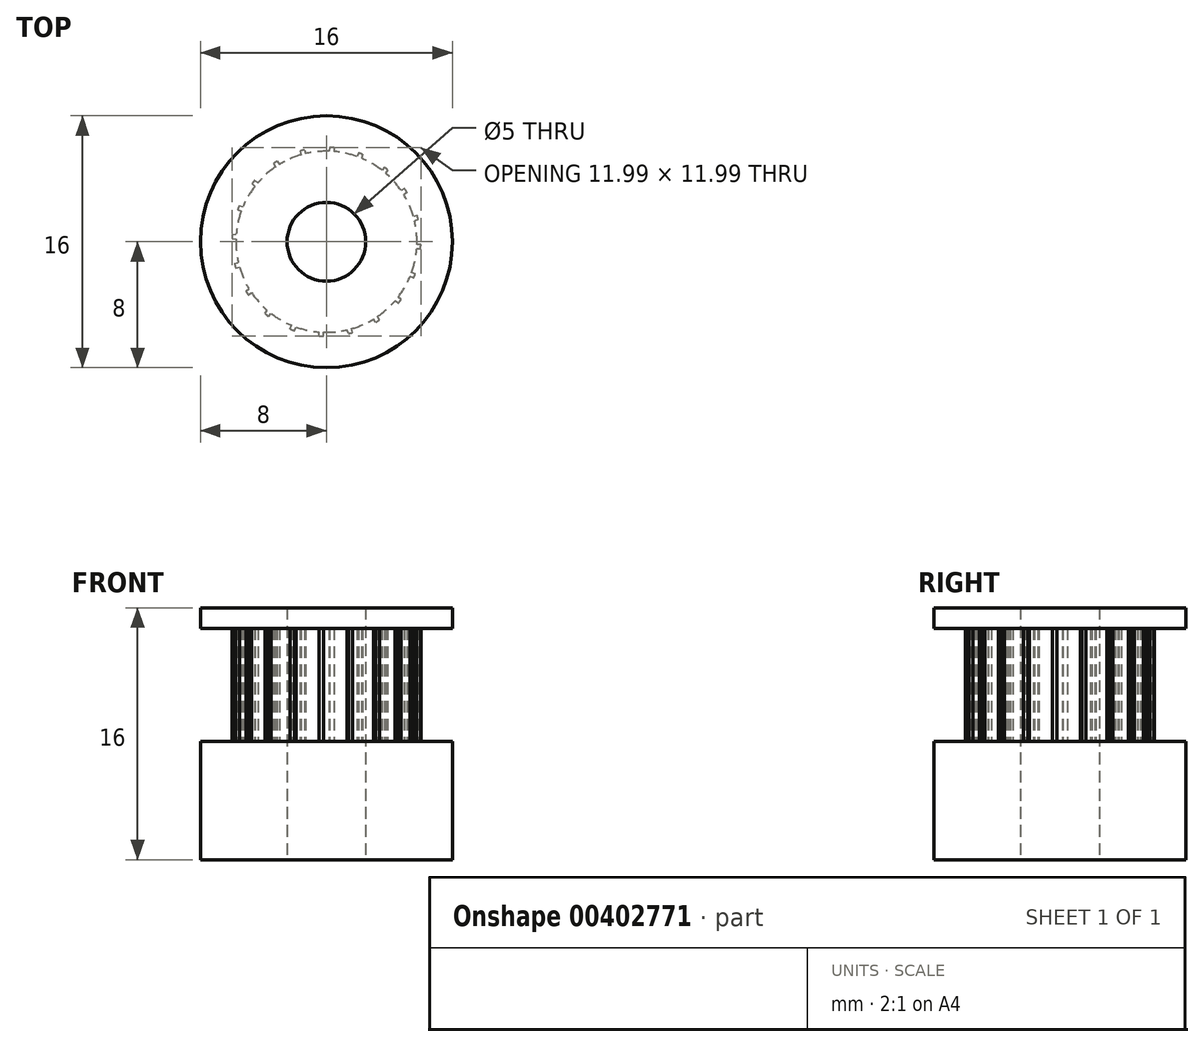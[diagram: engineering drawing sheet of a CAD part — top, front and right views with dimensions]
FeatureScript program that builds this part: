
annotation { "Feature Type Name" : "Feature", "Feature Type Description" : "" }
export const myFeature = defineFeature(function(context is Context, id is Id, definition is map)
    precondition{}
    {
        {
            var Q0;
            Q0=qCreatedBy(makeId("Top.planeOp"),FACE);
            var sketch = newSketch(context, id + "F0", { "sketchPlane" : qUnion([Q0])});
            skCircle(sketch, "E0", {"center": v(0, 0) * mm, "radius": 8 * mm});
            skCircle(sketch, "E1", {"center": v(0, 0) * mm, "radius": 2.5 * mm});
            skSolve(sketch);
        }
        {
            var Q0;
            Q0=makeQuery(id+"F0.imprint","IMPRINT",FACE,{"disambiguationData":[TD([[makeQuery(id+"F0.imprint","IMPRINT",EDGE,{"derivedFrom":sQuery(id+"F0.wireOp",EDGE,"E0")}),1.0]])]});
            extrude(context, id + "F1", {"entities" : qUnion([Q0]), "depth" : 7.5 * mm});
        }
        {
            var Q0;
            Q0=makeQuery(id+"F1.opExtrude","CAP_FACE",FACE,{"disambiguationData":[OSD([sQuery(id+"F0.wireOp",EDGE,"E0"),sQuery(id+"F0.wireOp",EDGE,"E1")])],"isStart":false});
            var sketch = newSketch(context, id + "F2", { "sketchPlane" : qUnion([Q0])});
            skArc(sketch, "E2", {"start": v(5.12, 3.13) * mm, "mid": v(5.04, 3.25) * mm, "end": v(4.96, 3.37) * mm});
            skArc(sketch, "E3", {"start": v(5.52, 1.6) * mm, "mid": v(5.26, 2.32) * mm, "end": v(4.92, 2.98) * mm});
            skLineSegment(sketch, "E4", {"start": v(4.96, 3.37) * mm, "end": v(4.75, 3.24) * mm});
            skLineSegment(sketch, "E5", {"start": v(3.9, 4.56) * mm, "end": v(3.75, 4.36) * mm});
            skLineSegment(sketch, "E6.1.0", {"start": v(2.3, 5.54) * mm, "end": v(2.22, 5.3) * mm});
            skLineSegment(sketch, "E6.1.1", {"start": v(3.68, 4.74) * mm, "end": v(3.52, 4.55) * mm});
            skLineSegment(sketch, "E6.2.0", {"start": v(0.47, 5.98) * mm, "end": v(0.48, 5.73) * mm});
            skLineSegment(sketch, "E6.2.1", {"start": v(2.04, 5.64) * mm, "end": v(1.94, 5.41) * mm});
            skLineSegment(sketch, "E6.3.0", {"start": v(-1.4, 5.83) * mm, "end": v(-1.32, 5.6) * mm});
            skLineSegment(sketch, "E6.3.1", {"start": v(0.2, 6) * mm, "end": v(0.18, 5.75) * mm});
            skLineSegment(sketch, "E6.4.0", {"start": v(-3.13, 5.12) * mm, "end": v(-2.98, 4.92) * mm});
            skLineSegment(sketch, "E6.4.1", {"start": v(-1.67, 5.76) * mm, "end": v(-1.6, 5.52) * mm});
            skLineSegment(sketch, "E6.5.0", {"start": v(-4.56, 3.9) * mm, "end": v(-4.36, 3.75) * mm});
            skLineSegment(sketch, "E6.5.1", {"start": v(-3.37, 4.96) * mm, "end": v(-3.24, 4.75) * mm});
            skLineSegment(sketch, "E6.6.0", {"start": v(-5.54, 2.3) * mm, "end": v(-5.3, 2.22) * mm});
            skLineSegment(sketch, "E6.6.1", {"start": v(-4.74, 3.68) * mm, "end": v(-4.55, 3.52) * mm});
            skLineSegment(sketch, "E6.7.0", {"start": v(-5.98, 0.47) * mm, "end": v(-5.73, 0.48) * mm});
            skLineSegment(sketch, "E6.7.1", {"start": v(-5.64, 2.04) * mm, "end": v(-5.41, 1.94) * mm});
            skLineSegment(sketch, "E6.8.0", {"start": v(-5.83, -1.4) * mm, "end": v(-5.6, -1.32) * mm});
            skLineSegment(sketch, "E6.8.1", {"start": v(-6, 0.2) * mm, "end": v(-5.75, 0.18) * mm});
            skLineSegment(sketch, "E6.9.0", {"start": v(-5.12, -3.13) * mm, "end": v(-4.92, -2.98) * mm});
            skLineSegment(sketch, "E6.9.1", {"start": v(-5.76, -1.67) * mm, "end": v(-5.52, -1.6) * mm});
            skLineSegment(sketch, "E6.10.0", {"start": v(-3.9, -4.56) * mm, "end": v(-3.75, -4.36) * mm});
            skLineSegment(sketch, "E6.10.1", {"start": v(-4.96, -3.37) * mm, "end": v(-4.75, -3.24) * mm});
            skLineSegment(sketch, "E6.11.0", {"start": v(-2.3, -5.54) * mm, "end": v(-2.22, -5.3) * mm});
            skLineSegment(sketch, "E6.11.1", {"start": v(-3.68, -4.74) * mm, "end": v(-3.52, -4.55) * mm});
            skLineSegment(sketch, "E6.12.0", {"start": v(-0.47, -5.98) * mm, "end": v(-0.48, -5.73) * mm});
            skLineSegment(sketch, "E6.12.1", {"start": v(-2.04, -5.64) * mm, "end": v(-1.94, -5.41) * mm});
            skLineSegment(sketch, "E6.13.0", {"start": v(1.4, -5.83) * mm, "end": v(1.32, -5.6) * mm});
            skLineSegment(sketch, "E6.13.1", {"start": v(-0.2, -6) * mm, "end": v(-0.18, -5.75) * mm});
            skLineSegment(sketch, "E6.14.0", {"start": v(3.13, -5.12) * mm, "end": v(2.98, -4.92) * mm});
            skLineSegment(sketch, "E6.14.1", {"start": v(1.67, -5.76) * mm, "end": v(1.6, -5.52) * mm});
            skLineSegment(sketch, "E6.15.0", {"start": v(4.56, -3.9) * mm, "end": v(4.36, -3.75) * mm});
            skLineSegment(sketch, "E6.15.1", {"start": v(3.37, -4.96) * mm, "end": v(3.24, -4.75) * mm});
            skLineSegment(sketch, "E6.16.0", {"start": v(5.54, -2.3) * mm, "end": v(5.3, -2.22) * mm});
            skLineSegment(sketch, "E6.16.1", {"start": v(4.74, -3.68) * mm, "end": v(4.55, -3.52) * mm});
            skLineSegment(sketch, "E6.17.0", {"start": v(5.98, -0.47) * mm, "end": v(5.73, -0.48) * mm});
            skLineSegment(sketch, "E6.17.1", {"start": v(5.64, -2.04) * mm, "end": v(5.41, -1.94) * mm});
            skLineSegment(sketch, "E6.18.0", {"start": v(5.83, 1.4) * mm, "end": v(5.6, 1.32) * mm});
            skLineSegment(sketch, "E6.18.1", {"start": v(6, -0.2) * mm, "end": v(5.75, -0.18) * mm});
            skLineSegment(sketch, "E6.19.0", {"start": v(5.12, 3.13) * mm, "end": v(4.92, 2.98) * mm});
            skLineSegment(sketch, "E6.19.1", {"start": v(5.76, 1.67) * mm, "end": v(5.52, 1.6) * mm});
            skArc(sketch, "E7.trimOffspring", {"start": v(3.9, 4.56) * mm, "mid": v(3.8, 4.65) * mm, "end": v(3.68, 4.74) * mm});
            skArc(sketch, "E8.trimOffspring", {"start": v(2.3, 5.54) * mm, "mid": v(2.17, 5.6) * mm, "end": v(2.04, 5.64) * mm});
            skArc(sketch, "E9.trimOffspring", {"start": v(0.47, 5.98) * mm, "mid": v(0.33, 6) * mm, "end": v(0.2, 6) * mm});
            skArc(sketch, "E10.trimOffspring", {"start": v(-1.4, 5.83) * mm, "mid": v(-1.54, 5.8) * mm, "end": v(-1.67, 5.76) * mm});
            skArc(sketch, "E11.trimOffspring", {"start": v(-3.13, 5.12) * mm, "mid": v(-3.25, 5.04) * mm, "end": v(-3.37, 4.96) * mm});
            skArc(sketch, "E12.trimOffspring", {"start": v(-4.56, 3.9) * mm, "mid": v(-4.65, 3.8) * mm, "end": v(-4.74, 3.68) * mm});
            skArc(sketch, "E13.trimOffspring", {"start": v(-5.54, 2.3) * mm, "mid": v(-5.6, 2.17) * mm, "end": v(-5.64, 2.04) * mm});
            skArc(sketch, "E14.trimOffspring", {"start": v(-5.98, 0.47) * mm, "mid": v(-6, 0.33) * mm, "end": v(-6, 0.2) * mm});
            skArc(sketch, "E15.trimOffspring", {"start": v(-5.83, -1.4) * mm, "mid": v(-5.8, -1.54) * mm, "end": v(-5.76, -1.67) * mm});
            skArc(sketch, "E16.trimOffspring", {"start": v(-5.12, -3.13) * mm, "mid": v(-5.04, -3.25) * mm, "end": v(-4.96, -3.37) * mm});
            skArc(sketch, "E17.trimOffspring", {"start": v(-3.9, -4.56) * mm, "mid": v(-3.8, -4.65) * mm, "end": v(-3.68, -4.74) * mm});
            skArc(sketch, "E18.trimOffspring", {"start": v(-2.3, -5.54) * mm, "mid": v(-2.17, -5.6) * mm, "end": v(-2.04, -5.64) * mm});
            skArc(sketch, "E19.trimOffspring", {"start": v(-0.47, -5.98) * mm, "mid": v(-0.33, -6) * mm, "end": v(-0.2, -6) * mm});
            skArc(sketch, "E20.trimOffspring", {"start": v(1.4, -5.83) * mm, "mid": v(1.54, -5.8) * mm, "end": v(1.67, -5.76) * mm});
            skArc(sketch, "E21.trimOffspring", {"start": v(3.13, -5.12) * mm, "mid": v(3.25, -5.04) * mm, "end": v(3.37, -4.96) * mm});
            skArc(sketch, "E22.trimOffspring", {"start": v(4.56, -3.9) * mm, "mid": v(4.65, -3.8) * mm, "end": v(4.74, -3.68) * mm});
            skArc(sketch, "E23.trimOffspring", {"start": v(5.54, -2.3) * mm, "mid": v(5.6, -2.17) * mm, "end": v(5.64, -2.04) * mm});
            skArc(sketch, "E24.trimOffspring", {"start": v(5.98, -0.47) * mm, "mid": v(6, -0.33) * mm, "end": v(6, -0.2) * mm});
            skArc(sketch, "E25.trimOffspring", {"start": v(5.83, 1.4) * mm, "mid": v(5.8, 1.54) * mm, "end": v(5.76, 1.67) * mm});
            skArc(sketch, "E26.trimOffspring", {"start": v(5.75, -0.18) * mm, "mid": v(5.72, 0.58) * mm, "end": v(5.6, 1.32) * mm});
            skArc(sketch, "E27.trimOffspring", {"start": v(5.41, -1.94) * mm, "mid": v(5.62, -1.22) * mm, "end": v(5.73, -0.48) * mm});
            skArc(sketch, "E28.trimOffspring", {"start": v(4.55, -3.52) * mm, "mid": v(4.97, -2.9) * mm, "end": v(5.3, -2.22) * mm});
            skArc(sketch, "E29.trimOffspring", {"start": v(3.24, -4.75) * mm, "mid": v(3.83, -4.3) * mm, "end": v(4.36, -3.75) * mm});
            skArc(sketch, "E30.trimOffspring", {"start": v(1.6, -5.52) * mm, "mid": v(2.32, -5.26) * mm, "end": v(2.98, -4.92) * mm});
            skArc(sketch, "E31.trimOffspring", {"start": v(-0.18, -5.75) * mm, "mid": v(0.58, -5.72) * mm, "end": v(1.32, -5.6) * mm});
            skArc(sketch, "E32.trimOffspring", {"start": v(-1.94, -5.41) * mm, "mid": v(-1.22, -5.62) * mm, "end": v(-0.48, -5.73) * mm});
            skArc(sketch, "E33.trimOffspring", {"start": v(-3.52, -4.55) * mm, "mid": v(-2.9, -4.97) * mm, "end": v(-2.22, -5.3) * mm});
            skArc(sketch, "E34.trimOffspring", {"start": v(-4.75, -3.24) * mm, "mid": v(-4.3, -3.83) * mm, "end": v(-3.75, -4.36) * mm});
            skArc(sketch, "E35.trimOffspring", {"start": v(-5.52, -1.6) * mm, "mid": v(-5.26, -2.32) * mm, "end": v(-4.92, -2.98) * mm});
            skArc(sketch, "E36.trimOffspring", {"start": v(-5.75, 0.18) * mm, "mid": v(-5.72, -0.58) * mm, "end": v(-5.6, -1.32) * mm});
            skArc(sketch, "E37.trimOffspring", {"start": v(-5.41, 1.94) * mm, "mid": v(-5.62, 1.22) * mm, "end": v(-5.73, 0.48) * mm});
            skArc(sketch, "E38.trimOffspring", {"start": v(-4.55, 3.52) * mm, "mid": v(-4.97, 2.9) * mm, "end": v(-5.3, 2.22) * mm});
            skArc(sketch, "E39.trimOffspring", {"start": v(-3.24, 4.75) * mm, "mid": v(-3.83, 4.3) * mm, "end": v(-4.36, 3.75) * mm});
            skArc(sketch, "E40.trimOffspring", {"start": v(-1.6, 5.52) * mm, "mid": v(-2.32, 5.26) * mm, "end": v(-2.98, 4.92) * mm});
            skArc(sketch, "E41.trimOffspring", {"start": v(0.18, 5.75) * mm, "mid": v(-0.58, 5.72) * mm, "end": v(-1.32, 5.6) * mm});
            skArc(sketch, "E42.trimOffspring", {"start": v(1.94, 5.41) * mm, "mid": v(1.22, 5.62) * mm, "end": v(0.48, 5.73) * mm});
            skArc(sketch, "E43.trimOffspring", {"start": v(3.52, 4.55) * mm, "mid": v(2.9, 4.97) * mm, "end": v(2.22, 5.3) * mm});
            skArc(sketch, "E44.trimOffspring", {"start": v(4.75, 3.24) * mm, "mid": v(4.3, 3.83) * mm, "end": v(3.75, 4.36) * mm});
            skSolve(sketch);
        }
        {
            var Q0;
            Q0=makeQuery(id+"F2.imprint","IMPRINT",FACE,{"disambiguationData":[TD([[makeQuery(id+"F2.imprint","IMPRINT",EDGE,{"derivedFrom":sQuery(id+"F2.wireOp",EDGE,"E2")}),1.0]])]});
            extrude(context, id + "F3", {"entities" : qUnion([Q0]), "operationType" : NewBodyOperationType.ADD, "depth" : 7.2 * mm});
        }
        {
            var Q0;
            Q0=makeQuery(id+"F3.opExtrude","CAP_FACE",FACE,{"disambiguationData":[OSD([sQuery(id+"F0.wireOp",EDGE,"E1"),sQuery(id+"F2.wireOp",EDGE,"E2"),sQuery(id+"F2.wireOp",EDGE,"E3"),sQuery(id+"F2.wireOp",EDGE,"E4"),sQuery(id+"F2.wireOp",EDGE,"E5"),sQuery(id+"F2.wireOp",EDGE,"E6.1.0"),sQuery(id+"F2.wireOp",EDGE,"E6.1.1"),sQuery(id+"F2.wireOp",EDGE,"E6.2.0"),sQuery(id+"F2.wireOp",EDGE,"E6.2.1"),sQuery(id+"F2.wireOp",EDGE,"E6.3.0"),sQuery(id+"F2.wireOp",EDGE,"E6.3.1"),sQuery(id+"F2.wireOp",EDGE,"E6.4.0"),sQuery(id+"F2.wireOp",EDGE,"E6.4.1"),sQuery(id+"F2.wireOp",EDGE,"E6.5.0"),sQuery(id+"F2.wireOp",EDGE,"E6.5.1"),sQuery(id+"F2.wireOp",EDGE,"E6.6.0"),sQuery(id+"F2.wireOp",EDGE,"E6.6.1"),sQuery(id+"F2.wireOp",EDGE,"E6.7.0"),sQuery(id+"F2.wireOp",EDGE,"E6.7.1"),sQuery(id+"F2.wireOp",EDGE,"E6.8.0"),sQuery(id+"F2.wireOp",EDGE,"E6.8.1"),sQuery(id+"F2.wireOp",EDGE,"E6.9.0"),sQuery(id+"F2.wireOp",EDGE,"E6.9.1"),sQuery(id+"F2.wireOp",EDGE,"E6.10.0"),sQuery(id+"F2.wireOp",EDGE,"E6.10.1"),sQuery(id+"F2.wireOp",EDGE,"E6.11.0"),sQuery(id+"F2.wireOp",EDGE,"E6.11.1"),sQuery(id+"F2.wireOp",EDGE,"E6.12.0"),sQuery(id+"F2.wireOp",EDGE,"E6.12.1"),sQuery(id+"F2.wireOp",EDGE,"E6.13.0"),sQuery(id+"F2.wireOp",EDGE,"E6.13.1"),sQuery(id+"F2.wireOp",EDGE,"E6.14.0"),sQuery(id+"F2.wireOp",EDGE,"E6.14.1"),sQuery(id+"F2.wireOp",EDGE,"E6.15.0"),sQuery(id+"F2.wireOp",EDGE,"E6.15.1"),sQuery(id+"F2.wireOp",EDGE,"E6.16.0"),sQuery(id+"F2.wireOp",EDGE,"E6.16.1"),sQuery(id+"F2.wireOp",EDGE,"E6.17.0"),sQuery(id+"F2.wireOp",EDGE,"E6.17.1"),sQuery(id+"F2.wireOp",EDGE,"E6.18.0"),sQuery(id+"F2.wireOp",EDGE,"E6.18.1"),sQuery(id+"F2.wireOp",EDGE,"E6.19.0"),sQuery(id+"F2.wireOp",EDGE,"E6.19.1"),sQuery(id+"F2.wireOp",EDGE,"E7.trimOffspring"),sQuery(id+"F2.wireOp",EDGE,"E8.trimOffspring"),sQuery(id+"F2.wireOp",EDGE,"E9.trimOffspring"),sQuery(id+"F2.wireOp",EDGE,"E10.trimOffspring"),sQuery(id+"F2.wireOp",EDGE,"E11.trimOffspring"),sQuery(id+"F2.wireOp",EDGE,"E12.trimOffspring"),sQuery(id+"F2.wireOp",EDGE,"E13.trimOffspring"),sQuery(id+"F2.wireOp",EDGE,"E14.trimOffspring"),sQuery(id+"F2.wireOp",EDGE,"E15.trimOffspring"),sQuery(id+"F2.wireOp",EDGE,"E16.trimOffspring"),sQuery(id+"F2.wireOp",EDGE,"E17.trimOffspring"),sQuery(id+"F2.wireOp",EDGE,"E18.trimOffspring"),sQuery(id+"F2.wireOp",EDGE,"E19.trimOffspring"),sQuery(id+"F2.wireOp",EDGE,"E20.trimOffspring"),sQuery(id+"F2.wireOp",EDGE,"E21.trimOffspring"),sQuery(id+"F2.wireOp",EDGE,"E22.trimOffspring"),sQuery(id+"F2.wireOp",EDGE,"E23.trimOffspring"),sQuery(id+"F2.wireOp",EDGE,"E24.trimOffspring"),sQuery(id+"F2.wireOp",EDGE,"E25.trimOffspring"),sQuery(id+"F2.wireOp",EDGE,"E26.trimOffspring"),sQuery(id+"F2.wireOp",EDGE,"E27.trimOffspring"),sQuery(id+"F2.wireOp",EDGE,"E28.trimOffspring"),sQuery(id+"F2.wireOp",EDGE,"E29.trimOffspring"),sQuery(id+"F2.wireOp",EDGE,"E30.trimOffspring"),sQuery(id+"F2.wireOp",EDGE,"E31.trimOffspring"),sQuery(id+"F2.wireOp",EDGE,"E32.trimOffspring"),sQuery(id+"F2.wireOp",EDGE,"E33.trimOffspring"),sQuery(id+"F2.wireOp",EDGE,"E34.trimOffspring"),sQuery(id+"F2.wireOp",EDGE,"E35.trimOffspring"),sQuery(id+"F2.wireOp",EDGE,"E36.trimOffspring"),sQuery(id+"F2.wireOp",EDGE,"E37.trimOffspring"),sQuery(id+"F2.wireOp",EDGE,"E38.trimOffspring"),sQuery(id+"F2.wireOp",EDGE,"E39.trimOffspring"),sQuery(id+"F2.wireOp",EDGE,"E40.trimOffspring"),sQuery(id+"F2.wireOp",EDGE,"E41.trimOffspring"),sQuery(id+"F2.wireOp",EDGE,"E42.trimOffspring"),sQuery(id+"F2.wireOp",EDGE,"E43.trimOffspring"),sQuery(id+"F2.wireOp",EDGE,"E44.trimOffspring")])],"isStart":false});
            var sketch = newSketch(context, id + "F4", { "sketchPlane" : qUnion([Q0])});
            skCircle(sketch, "E45", {"center": v(0, 0) * mm, "radius": 8 * mm});
            skSolve(sketch);
        }
        {
            var Q0;
            Q0=makeQuery(id+"F4.imprint","IMPRINT",FACE,{"disambiguationData":[TD([[makeQuery(id+"F4.imprint","IMPRINT",EDGE,{"derivedFrom":makeQuery(id+"F3.opExtrude","CAP_EDGE",EDGE,{"disambiguationData":[OSD([sQuery(id+"F2.wireOp",EDGE,"E2")])],"isStart":false})}),1.0]])]});
            var Q1;
            Q1=makeQuery(id+"F4.imprint","IMPRINT",FACE,{"disambiguationData":[TD([[makeQuery(id+"F4.imprint","IMPRINT",EDGE,{"derivedFrom":sQuery(id+"F4.wireOp",EDGE,"E45")}),1.0]])]});
            extrude(context, id + "F5", {"entities" : qUnion([Q0, Q1]), "operationType" : NewBodyOperationType.ADD, "depth" : 1.3 * mm});
        }
    });
